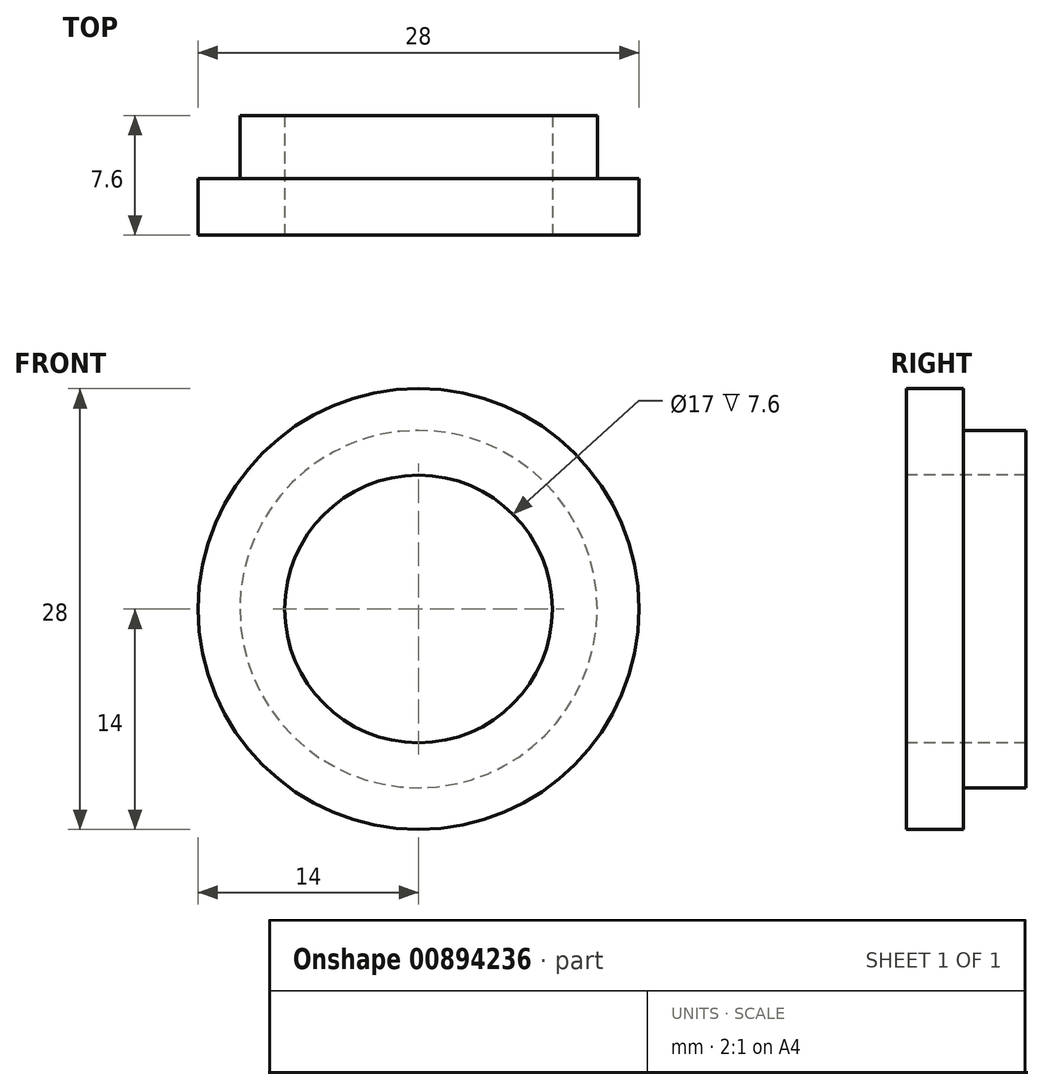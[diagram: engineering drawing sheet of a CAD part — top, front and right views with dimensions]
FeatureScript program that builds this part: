
annotation { "Feature Type Name" : "Feature", "Feature Type Description" : "" }
export const myFeature = defineFeature(function(context is Context, id is Id, definition is map)
    precondition{}
    {
        {
            var Q0;
            Q0=qCreatedBy(makeId("Right.planeOp"),FACE);
            var sketch = newSketch(context, id + "F0", { "sketchPlane" : qUnion([Q0])});
            skLineSegment(sketch, "E0", {"start": v(0, 0) * mm, "end": v(0, 8.5) * mm, "construction": true});
            skLineSegment(sketch, "E1", {"start": v(0, 8.5) * mm, "end": v(7.6, 8.5) * mm});
            skLineSegment(sketch, "E2", {"start": v(7.6, 8.5) * mm, "end": v(7.6, 11.35) * mm});
            skLineSegment(sketch, "E3", {"start": v(7.6, 11.35) * mm, "end": v(3.6, 11.35) * mm});
            skLineSegment(sketch, "E4", {"start": v(3.6, 11.35) * mm, "end": v(3.6, 14) * mm});
            skLineSegment(sketch, "E5", {"start": v(3.6, 14) * mm, "end": v(0, 14) * mm});
            skLineSegment(sketch, "E6", {"start": v(0, 14) * mm, "end": v(0, 8.5) * mm});
            skLineSegment(sketch, "E7", {"start": v(0, 0) * mm, "end": v(7.6, 0) * mm});
            skSolve(sketch);
        }
        {
            var Q0;
            Q0=makeQuery(id+"F0.imprint","IMPRINT",FACE,{"disambiguationData":[TD([[makeQuery(id+"F0.imprint","IMPRINT",EDGE,{"derivedFrom":sQuery(id+"F0.wireOp",EDGE,"E1")}),1.0]])]});
            var Q1;
            Q1=sQuery(id+"F0.wireOp",EDGE,"E7");
            revolve(context, id + "F1", {"surfaceOperationType" : NewSurfaceOperationType.NEW, "entities" : qUnion([Q0]), "axis" : qUnion([Q1]), "revolveType" : RevolveType.FULL});
        }
    });
